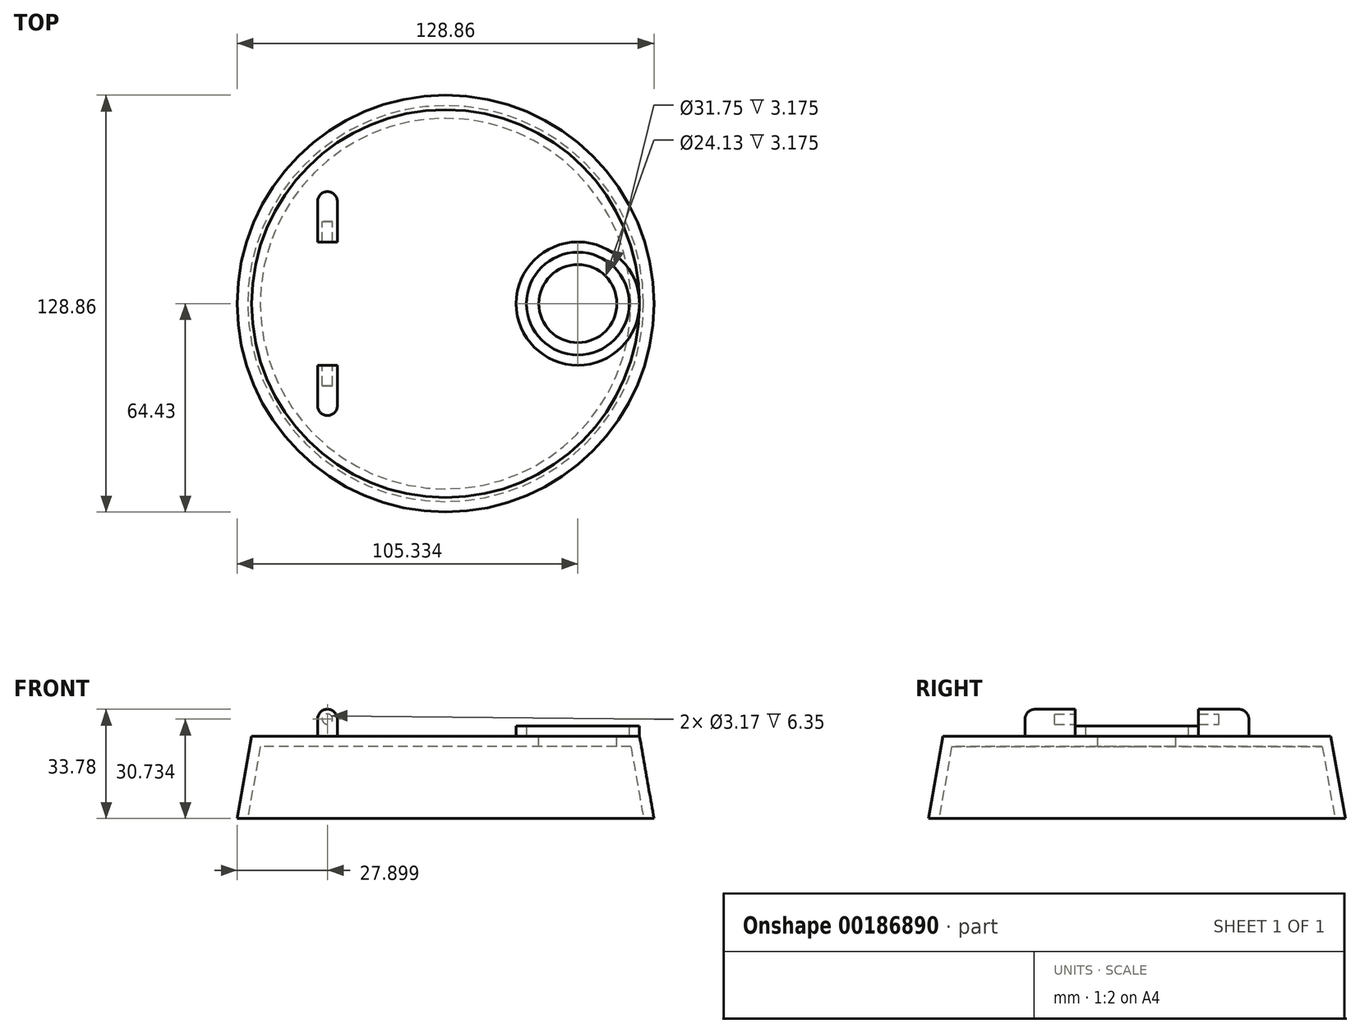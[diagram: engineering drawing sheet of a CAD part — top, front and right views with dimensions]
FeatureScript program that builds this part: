
annotation { "Feature Type Name" : "Feature", "Feature Type Description" : "" }
export const myFeature = defineFeature(function(context is Context, id is Id, definition is map)
    precondition{}
    {
        {
            var Q0;
            Q0=qCreatedBy(makeId("Top.planeOp"),FACE);
            var sketch = newSketch(context, id + "F0", { "sketchPlane" : qUnion([Q0])});
            skCircle(sketch, "E0", {"center": v(0, 0) * mm, "radius": 64.43 * mm});
            skSolve(sketch);
        }
        {
            var Q0;
            Q0=makeQuery(id+"F0.imprint","IMPRINT",FACE,{"disambiguationData":[TD([[makeQuery(id+"F0.imprint","IMPRINT",EDGE,{"derivedFrom":sQuery(id+"F0.wireOp",EDGE,"E0")}),1.0]])]});
            extrude(context, id + "F1", {"entities" : qUnion([Q0]), "depth" : 25.4 * mm, "hasDraft" : true, "draftAngle" : 10 * degree, "draftPullDirection" : true});
        }
        {
            var Q0;
            Q0=makeQuery(id+"F1.opExtrude","CAP_FACE",FACE,{"disambiguationData":[OSD([sQuery(id+"F0.wireOp",EDGE,"E0")])],"isStart":true});
            shell(context, id + "F2", {"entities" : qUnion([Q0]), "thickness" : 3.17 * mm});
        }
        {
            var Q0;
            Q0=makeQuery(id+"F1.opExtrude","CAP_FACE",FACE,{"disambiguationData":[OSD([sQuery(id+"F0.wireOp",EDGE,"E0")])],"isStart":false});
            var sketch = newSketch(context, id + "F3", { "sketchPlane" : qUnion([Q0])});
            skCircle(sketch, "E1", {"center": v(40.9, 0) * mm, "radius": 19.05 * mm});
            skCircle(sketch, "E2", {"center": v(40.9, 0) * mm, "radius": 15.88 * mm});
            skCircle(sketch, "E3", {"center": v(40.9, 0) * mm, "radius": 12.06 * mm});
            skSolve(sketch);
        }
        {
            var Q0;
            Q0=makeQuery(id+"F3.imprint","IMPRINT",FACE,{"disambiguationData":[TD([[makeQuery(id+"F3.imprint","IMPRINT",EDGE,{"derivedFrom":sQuery(id+"F3.wireOp",EDGE,"E1")}),1.0]])]});
            extrude(context, id + "F4", {"entities" : qUnion([Q0]), "operationType" : NewBodyOperationType.ADD, "depth" : 3.17 * mm});
        }
        {
            var Q0;
            Q0=makeQuery(id+"F3.imprint","IMPRINT",FACE,{"disambiguationData":[TD([[makeQuery(id+"F3.imprint","IMPRINT",EDGE,{"derivedFrom":sQuery(id+"F3.wireOp",EDGE,"E3")}),1.0]])]});
            extrude(context, id + "F5", {"entities" : qUnion([Q0]), "operationType" : NewBodyOperationType.REMOVE, "oppositeDirection" : true, "depth" : 25.4 * mm});
        }
        {
            var Q0;
            Q0=makeQuery(id+"F3.imprint","IMPRINT",FACE,{"disambiguationData":[TD([[makeQuery(id+"F3.imprint","IMPRINT",EDGE,{"derivedFrom":sQuery(id+"F3.wireOp",EDGE,"E1")}),-1.0]])]});
            var sketch = newSketch(context, id + "F6", { "sketchPlane" : qUnion([Q0])});
            skLineSegment(sketch, "E4", {"start": v(-33.48, -51.57) * mm, "end": v(-33.48, 80) * mm, "construction": true});
            skLineSegment(sketch, "E5.bottom", {"start": v(-33.48, -19.05) * mm, "end": v(-39.59, -19.05) * mm});
            skLineSegment(sketch, "E5.left", {"start": v(-33.48, -19.05) * mm, "end": v(-33.48, -31.56) * mm});
            skLineSegment(sketch, "E5.right", {"start": v(-39.59, -19.05) * mm, "end": v(-39.59, -31.56) * mm});
            skArc(sketch, "E6", {"start": v(-39.59, -31.56) * mm, "mid": v(-36.54, -34.61) * mm, "end": v(-33.48, -31.56) * mm});
            skLineSegment(sketch, "E7.MirrorCS", {"start": v(-39.59, 19.05) * mm, "end": v(-39.59, 31.56) * mm});
            skArc(sketch, "E8.MirrorCS", {"start": v(-39.59, 31.56) * mm, "mid": v(-36.54, 34.61) * mm, "end": v(-33.48, 31.56) * mm});
            skLineSegment(sketch, "E9.MirrorCS", {"start": v(-33.48, 51.57) * mm, "end": v(-33.48, -80) * mm, "construction": true});
            skLineSegment(sketch, "E10.MirrorCS", {"start": v(-33.48, 19.05) * mm, "end": v(-39.59, 19.05) * mm});
            skLineSegment(sketch, "E11.MirrorCS", {"start": v(-33.48, 19.05) * mm, "end": v(-33.48, 31.56) * mm});
            skSolve(sketch);
        }
        {
            var Q0;
            Q0 = qSketchRegion(id + "F6", true);
            extrude(context, id + "F7", {"entities" : qUnion([Q0]), "operationType" : NewBodyOperationType.ADD, "depth" : 8.38 * mm});
        }
        {
            var Q0;
            Q0=makeQuery(id+"F7.opExtrude","CAP_EDGE",EDGE,{"disambiguationData":[OSD([sQuery(id+"F6.wireOp",EDGE,"E5.left")])],"isStart":false});
            var Q1;
            Q1=makeQuery(id+"F7.opExtrude","CAP_EDGE",EDGE,{"disambiguationData":[OSD([sQuery(id+"F6.wireOp",EDGE,"E5.right")])],"isStart":false});
            var Q2;
            Q2=makeQuery(id+"F7.opExtrude","CAP_EDGE",EDGE,{"disambiguationData":[OSD([sQuery(id+"F6.wireOp",EDGE,"E6")])],"isStart":false});
            var Q3;
            Q3=makeQuery(id+"F7.opExtrude","CAP_EDGE",EDGE,{"disambiguationData":[OSD([sQuery(id+"F6.wireOp",EDGE,"E11.MirrorCS")])],"isStart":false});
            fillet(context, id + "F8", {"entities" : qUnion([Q0, Q1, Q2, Q3]), "radius" : 3.05 * mm, "tangentPropagation" : true, "allowEdgeOverflow" : false});
        }
        {
            var Q0;
            Q0=qCreatedBy(makeId("Front.planeOp"),FACE);
            var sketch = newSketch(context, id + "F9", { "sketchPlane" : qUnion([Q0])});
            skLineSegment(sketch, "E12.0.0", {"start": v(-36.53, 33.78) * mm, "end": v(-36.54, 33.78) * mm});
            skArc(sketch, "E12.0.1", {"start": v(-36.54, 33.78) * mm, "mid": v(-38.7, 32.89) * mm, "end": v(-39.59, 30.73) * mm});
            skLineSegment(sketch, "E12.0.2", {"start": v(-39.59, 30.73) * mm, "end": v(-39.59, 25.4) * mm});
            skLineSegment(sketch, "E12.0.3", {"start": v(-39.59, 25.4) * mm, "end": v(-33.48, 25.4) * mm});
            skLineSegment(sketch, "E12.0.4", {"start": v(-33.48, 25.4) * mm, "end": v(-33.48, 30.73) * mm});
            skArc(sketch, "E12.0.5", {"start": v(-33.48, 30.73) * mm, "mid": v(-34.38, 32.89) * mm, "end": v(-36.53, 33.78) * mm});
            skCircle(sketch, "E13", {"center": v(-36.53, 30.73) * mm, "radius": 1.59 * mm});
            skSolve(sketch);
        }
        {
            var Q0;
            Q0=makeQuery(id+"F9.imprint","IMPRINT",FACE,{"disambiguationData":[TD([[makeQuery(id+"F9.imprint","IMPRINT",EDGE,{"derivedFrom":sQuery(id+"F9.wireOp",EDGE,"E13")}),1.0]])]});
            extrude(context, id + "F10", {"entities" : qUnion([Q0]), "operationType" : NewBodyOperationType.REMOVE, "depth" : 25.4 * mm, "hasSecondDirection" : true, "secondDirectionOppositeDirection" : true, "secondDirectionDepth" : 25.4 * mm});
        }
    });
